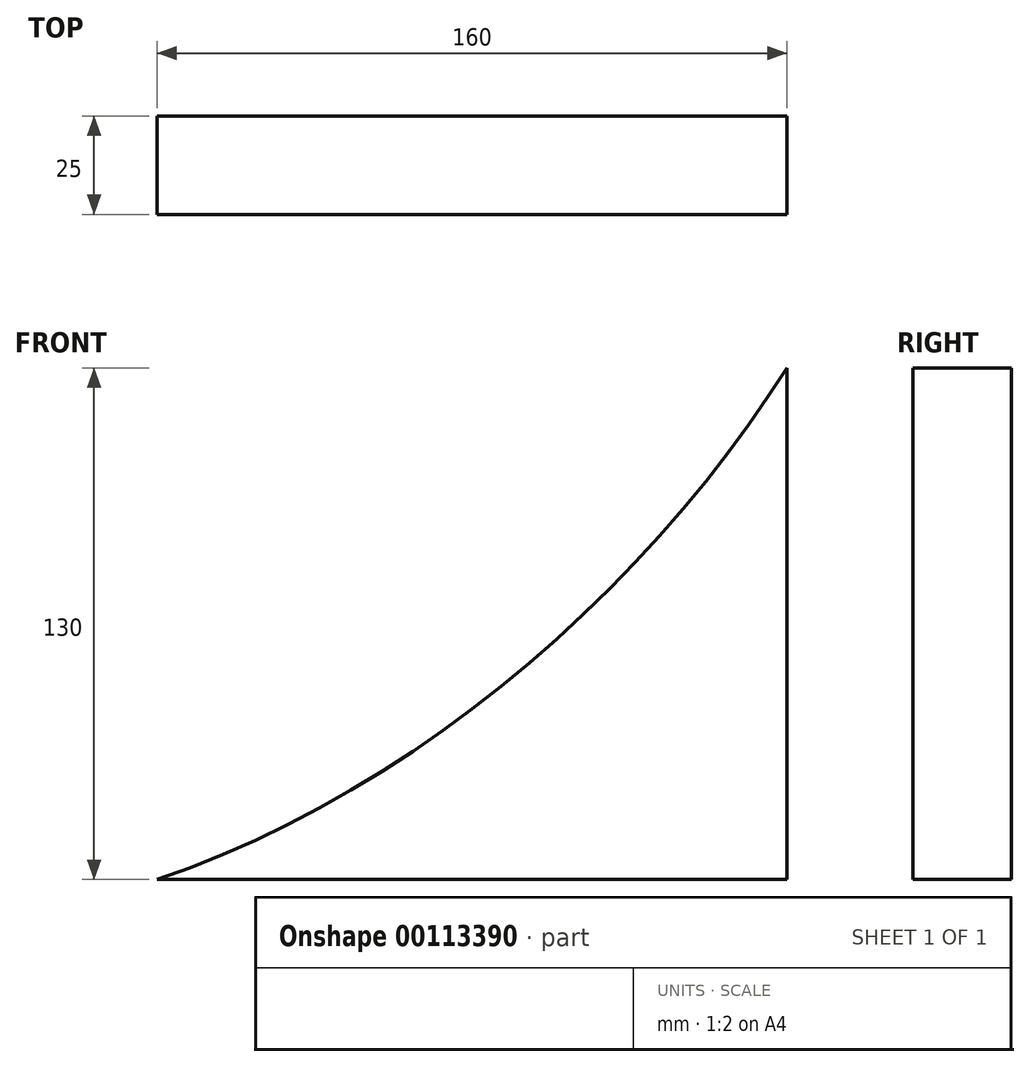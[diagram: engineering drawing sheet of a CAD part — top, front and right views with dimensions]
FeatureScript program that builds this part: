
annotation { "Feature Type Name" : "Feature", "Feature Type Description" : "" }
export const myFeature = defineFeature(function(context is Context, id is Id, definition is map)
    precondition{}
    {
        {
            var Q0;
            Q0=qCreatedBy(makeId("Front.planeOp"),FACE);
            var sketch = newSketch(context, id + "F0", { "sketchPlane" : qUnion([Q0])});
            skFitSpline(sketch, "E0", {"points": [v(-101.55, 64.1) * mm, v(-261.55, -65.9) * mm, v(-481.55, -65.9) * mm], "startDerivative": vector(-215.96, -343.22) * mm, "endDerivative": vector(-478.3, 74.11) * mm});
            skLineSegment(sketch, "E1", {"start": v(-101.55, 64.1) * mm, "end": v(-101.55, -65.9) * mm});
            skLineSegment(sketch, "E2", {"start": v(-101.55, -65.9) * mm, "end": v(-261.55, -65.9) * mm});
            skSolve(sketch);
        }
        {
            var Q0;
            Q0=makeQuery(id+"F0.imprint","IMPRINT",FACE,{"disambiguationData":[TD([[makeQuery(id+"F0.imprint","IMPRINT",EDGE,{"derivedFrom":sQuery(id+"F0.wireOp",EDGE,"E0")}),1.0]])]});
            extrude(context, id + "F1", {"entities" : qUnion([Q0]), "depth" : 25 * mm});
        }
    });
